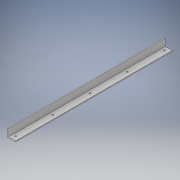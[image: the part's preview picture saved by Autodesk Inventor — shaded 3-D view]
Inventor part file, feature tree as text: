
AUTODESK INVENTOR PART (.ipt)
format: ipt  version: 2018 (Build 220112000, 112)  size: 121,344 bytes
history: native  units: in
note: dims shown in document units (in); Inventor stores cm internally (conversion verified against a paired STEP export)
features: extrude x2, sketch x2
ambient origin geometry x8: Origin, YZ Plane, XZ Plane, XY Plane, X Axis, Y Axis, Z Axis, Center Point
bodies: Solid1 (feature_tree)
feature tree (4):
  extrude  "Extrusion1"  Depth=1.0in
  extrude  "Extrusion3"  Depth=0.125in
  sketch  "Sketch1"  dims[d0=0.125in d1=1.0in]
  sketch  "Sketch2"  dims[d2=1.0in d3=0.125in d4=20.0in d5=0.0in d6=0.5in d7=0.5in d16=0.5in d29=21.0in d30=0.0in]
